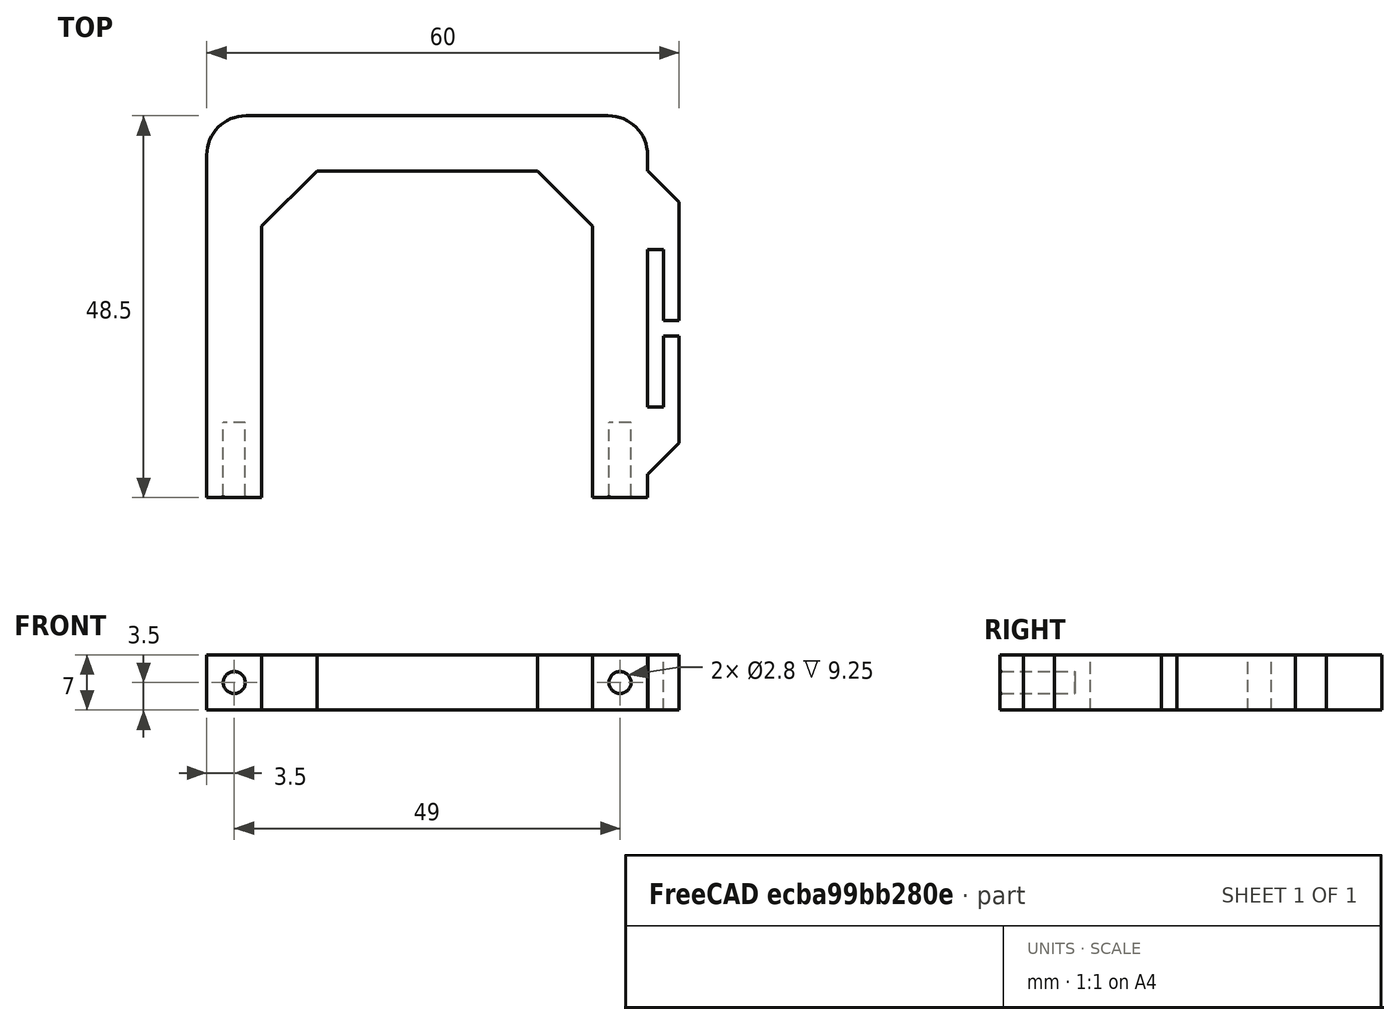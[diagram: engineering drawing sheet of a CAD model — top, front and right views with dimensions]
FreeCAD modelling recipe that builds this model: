
FCSTD DOCUMENT  (FreeCAD 0.14R3703 (Git))
Label: GOUM_Extruder_Holder_Part2
License: CC-BY 3.0
LicenseURL: http://creativecommons.org/licenses/by/3.0/
objects: Part::Box×6, Part::Cut×4, Part::Cylinder×2, Part::Chamfer×2, Part::Fillet×2, Part::MultiFuse×1
note: 17 computed .brp shape members not serialized (recipe doc carries the construction recipe); baked Part::Feature solids carry a one-line shape summary decoded from their .brp

FEATURE [Part::Box] Box  label="Base"
  Height = 7
  Length = 42
  Width = 7
FEATURE [Part::Box] Box001  label="Side1"
  Height = 7
  Length = 7
  Placement = pos=(-7,-41.5,0) rot=(0,0,1;0rad)
  Width = 48.5
FEATURE [Part::Box] Box002  label="Side2"
  Height = 7
  Length = 7
  Placement = pos=(42,-41.5,0) rot=(0,0,1;0rad)
  Width = 48.5
FEATURE [Part::Box] Box003  label="cable-slot"
  Height = 7
  Length = 2
  Placement = pos=(49,-30,0) rot=(0,0,1;0rad)
  Width = 20
FEATURE [Part::Box] Box004  label="cable-support"
  Height = 7
  Length = 4
  Placement = pos=(49,-38.5,0) rot=(0,0,1;0rad)
  Width = 38.5
FEATURE [Part::Box] Box005  label="cable-slot2"
  Height = 7
  Length = 2
  Placement = pos=(51,-21,0) rot=(0,0,1;0rad)
  Width = 2
FEATURE [Part::Cylinder] Cylinder  label="Bolt1"
  Angle = 360
  Height = 10
  Placement = pos=(-3.5,-42,3.5) rot=(-1,0,0;1.5708rad)
  Radius = 1.4
FEATURE [Part::Cylinder] Cylinder001  label="Bolt2"
  Angle = 360
  Height = 10
  Placement = pos=(45.5,-42,3.5) rot=(-1,0,0;1.5708rad)
  Radius = 1.4
FEATURE [Part::MultiFuse] Fusion
  Shapes = -> [Box,Box001,Box002,Box004]
FEATURE [Part::Cut] Cut
  Base = -> Fusion
  Tool = -> Box003
FEATURE [Part::Cut] Cut001
  Base = -> Cut
  Tool = -> Box005
FEATURE [Part::Cut] Cut002
  Base = -> Cut001
  Tool = -> Cylinder
FEATURE [Part::Cut] Cut003
  Base = -> Cut002
  Tool = -> Cylinder001
FEATURE [Part::Chamfer] Chamfer
  Base = -> Cut003
  Edges = 2 edges r=3.95: [Edge4,Edge67]
FEATURE [Part::Chamfer] Chamfer001
  Base = -> Chamfer
  Edges = 2 edges r=7: [Edge39,Edge64]
FEATURE [Part::Fillet] Fillet
  Base = -> Chamfer001
  Edges = 2 edges r=5: [Edge27,Edge92]
FEATURE [Part::Fillet] Fillet001  label="Holder-clamp"
  Base = -> Fillet
  Edges = 2 edges r=0.25: [Edge39,Edge100]
